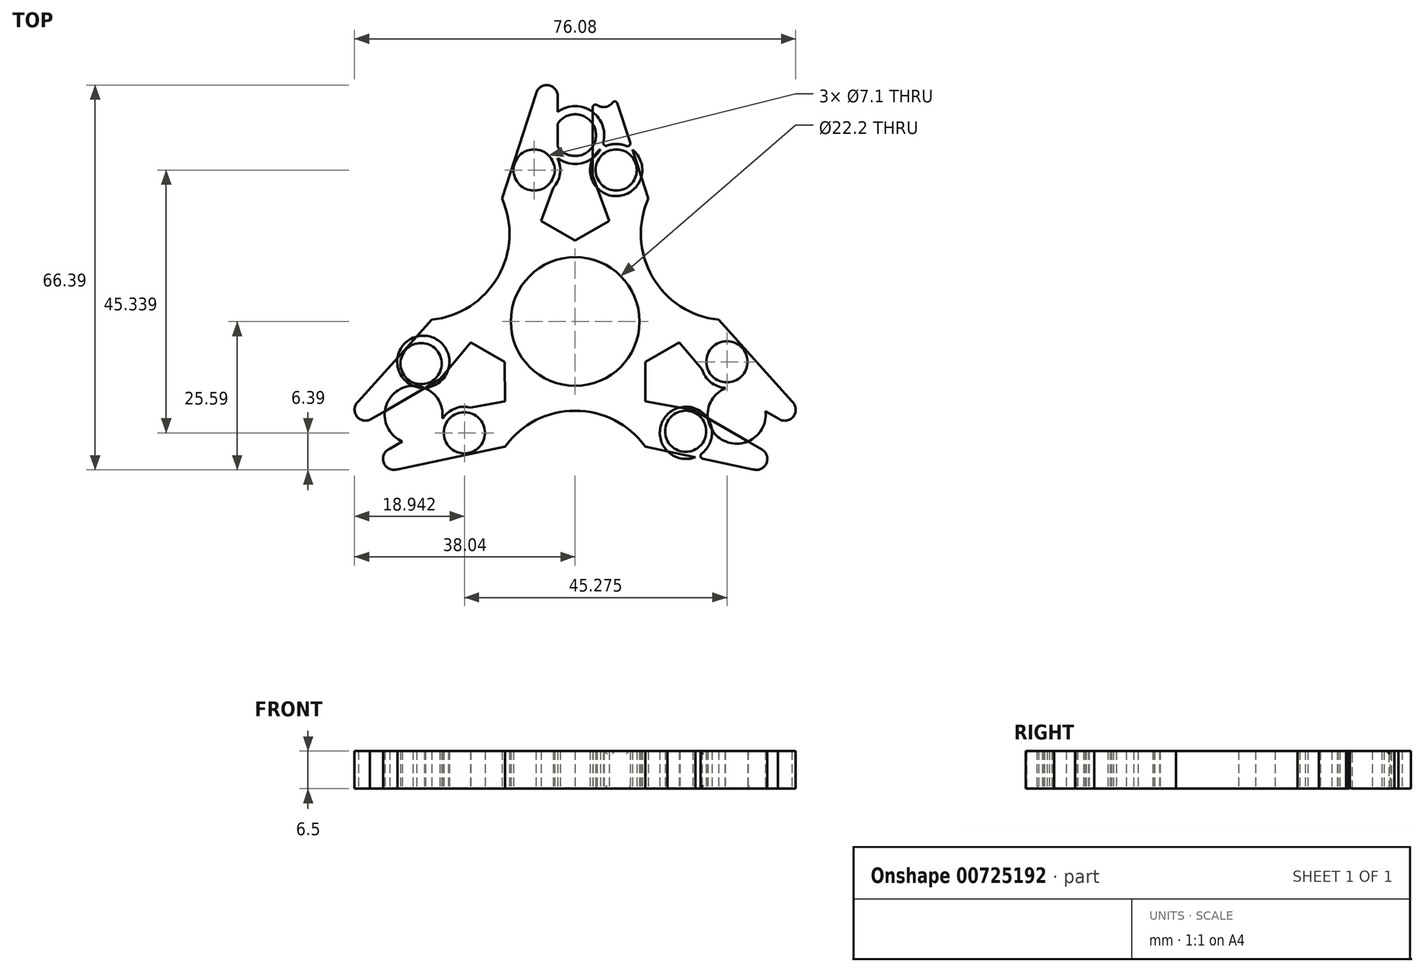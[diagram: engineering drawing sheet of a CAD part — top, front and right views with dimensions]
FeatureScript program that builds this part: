
annotation { "Feature Type Name" : "Feature", "Feature Type Description" : "" }
export const myFeature = defineFeature(function(context is Context, id is Id, definition is map)
    precondition{}
    {
        {
            var Q0;
            Q0=qCreatedBy(makeId("Top.planeOp"),FACE);
            var sketch = newSketch(context, id + "F0", { "sketchPlane" : qUnion([Q0])});
            skCircle(sketch, "E0", {"center": v(0, 0) * mm, "radius": 11.1 * mm});
            skCircle(sketch, "E1", {"center": v(0, 0) * mm, "radius": 14 * mm});
            skPoint(sketch, "E2", {"position": v(-12.63, 21.25) * mm});
            skPoint(sketch, "E3", {"position": v(-6.76, 39.27) * mm});
            skPoint(sketch, "E4.MirrorP", {"position": v(6.76, 39.27) * mm});
            skPoint(sketch, "E5.MirrorP", {"position": v(12.63, 21.25) * mm});
            skLineSegment(sketch, "E6", {"start": v(-12.63, 21.25) * mm, "end": v(-6.76, 39.27) * mm});
            skLineSegment(sketch, "E7", {"start": v(6.76, 39.27) * mm, "end": v(12.63, 21.25) * mm});
            skPoint(sketch, "E8", {"position": v(-3.02, 39.15) * mm});
            skPoint(sketch, "E9", {"position": v(-3.02, 25.17) * mm});
            skPoint(sketch, "E10", {"position": v(-5.89, 17.35) * mm});
            skPoint(sketch, "E11", {"position": v(0, 14) * mm});
            skPoint(sketch, "E12.MirrorP", {"position": v(3.02, 39.15) * mm});
            skPoint(sketch, "E13.MirrorP", {"position": v(3.02, 25.17) * mm});
            skPoint(sketch, "E14.MirrorP", {"position": v(5.89, 17.35) * mm});
            skCircle(sketch, "E15", {"center": v(-4.9, 38.9) * mm, "radius": 1.9 * mm});
            skPoint(sketch, "E15.third.point", {"position": v(-3.58, 37.54) * mm});
            skCircle(sketch, "E16.MirrorC", {"center": v(4.9, 38.9) * mm, "radius": 1.9 * mm});
            skLineSegment(sketch, "E17", {"start": v(-3.02, 39.15) * mm, "end": v(-3.02, 25.17) * mm});
            skLineSegment(sketch, "E18", {"start": v(-5.89, 17.35) * mm, "end": v(-3.02, 25.17) * mm});
            skLineSegment(sketch, "E19", {"start": v(0, 14) * mm, "end": v(-5.89, 17.35) * mm});
            skLineSegment(sketch, "E20", {"start": v(0, 14) * mm, "end": v(5.89, 17.35) * mm});
            skLineSegment(sketch, "E21", {"start": v(3.02, 25.17) * mm, "end": v(5.89, 17.35) * mm});
            skLineSegment(sketch, "E22", {"start": v(3.02, 25.17) * mm, "end": v(3.02, 39.15) * mm});
            skCircle(sketch, "E23", {"center": v(-7.08, 26.14) * mm, "radius": 3.55 * mm});
            skCircle(sketch, "E24.MirrorC", {"center": v(7.08, 26.14) * mm, "radius": 3.55 * mm});
            skPoint(sketch, "E25.centerSnap0", {"position": v(-2.94, 15.68) * mm});
            skPoint(sketch, "E26", {"position": v(-3.02, 28.1) * mm});
            skPoint(sketch, "E27", {"position": v(-3.02, 34.99) * mm});
            skPoint(sketch, "E28.MirrorP", {"position": v(3.02, 34.99) * mm});
            skPoint(sketch, "E29.MirrorP", {"position": v(3.02, 28.1) * mm});
            skCircle(sketch, "E30", {"center": v(0, 32.16) * mm, "radius": 5 * mm});
            skPoint(sketch, "E30.centerSnap0", {"position": v(-3.02, 32.16) * mm});
            skCircle(sketch, "E31", {"center": v(0, 32.16) * mm, "radius": 3.6 * mm});
            skCircle(sketch, "E32.1.0", {"center": v(-31.24, -23.7) * mm, "radius": 1.9 * mm});
            skCircle(sketch, "E32.2.0", {"center": v(36.14, -15.2) * mm, "radius": 1.9 * mm});
            skCircle(sketch, "E33.1.0", {"center": v(-36.14, -15.2) * mm, "radius": 1.9 * mm});
            skCircle(sketch, "E33.2.0", {"center": v(31.24, -23.7) * mm, "radius": 1.9 * mm});
            skLineSegment(sketch, "E34.1.0", {"start": v(-12.09, -21.56) * mm, "end": v(-30.63, -25.5) * mm});
            skLineSegment(sketch, "E34.2.0", {"start": v(24.72, 0.31) * mm, "end": v(37.39, -13.78) * mm});
            skLineSegment(sketch, "E35.1.0", {"start": v(-37.39, -13.78) * mm, "end": v(-24.72, 0.31) * mm});
            skLineSegment(sketch, "E35.2.0", {"start": v(30.63, -25.5) * mm, "end": v(12.09, -21.56) * mm});
            skCircle(sketch, "E36.1.0", {"center": v(-19.1, -19.2) * mm, "radius": 3.55 * mm});
            skCircle(sketch, "E36.2.0", {"center": v(26.18, -6.94) * mm, "radius": 3.55 * mm});
            skCircle(sketch, "E37.1.1", {"center": v(-26.57, -7.25) * mm, "radius": 3.55 * mm});
            skLineSegment(sketch, "E37.1.3", {"start": v(-23.31, -9.97) * mm, "end": v(-17.97, -3.58) * mm});
            skLineSegment(sketch, "E37.1.4", {"start": v(-12.12, -7) * mm, "end": v(-17.97, -3.58) * mm});
            skLineSegment(sketch, "E37.1.5", {"start": v(-12.12, -7) * mm, "end": v(-12.09, -13.77) * mm});
            skLineSegment(sketch, "E37.1.6", {"start": v(-12.09, -13.77) * mm, "end": v(-20.3, -15.2) * mm});
            skLineSegment(sketch, "E37.1.7", {"start": v(-32.4, -22.19) * mm, "end": v(-20.3, -15.2) * mm});
            skCircle(sketch, "E37.1.8", {"center": v(-27.85, -16.08) * mm, "radius": 5 * mm});
            skCircle(sketch, "E37.1.9", {"center": v(-27.85, -16.08) * mm, "radius": 3.6 * mm});
            skLineSegment(sketch, "E37.1.10", {"start": v(-23.31, -9.97) * mm, "end": v(-35.41, -16.96) * mm});
            skCircle(sketch, "E37.2.1", {"center": v(19.05, -18.93) * mm, "radius": 3.55 * mm});
            skLineSegment(sketch, "E37.2.3", {"start": v(20.3, -15.2) * mm, "end": v(12.09, -13.77) * mm});
            skLineSegment(sketch, "E37.2.4", {"start": v(12.12, -7) * mm, "end": v(12.09, -13.77) * mm});
            skLineSegment(sketch, "E37.2.5", {"start": v(12.12, -7) * mm, "end": v(17.97, -3.58) * mm});
            skLineSegment(sketch, "E37.2.6", {"start": v(17.97, -3.58) * mm, "end": v(23.31, -9.97) * mm});
            skLineSegment(sketch, "E37.2.7", {"start": v(35.41, -16.96) * mm, "end": v(23.31, -9.97) * mm});
            skCircle(sketch, "E37.2.8", {"center": v(27.85, -16.08) * mm, "radius": 5 * mm});
            skCircle(sketch, "E37.2.9", {"center": v(27.85, -16.08) * mm, "radius": 3.6 * mm});
            skLineSegment(sketch, "E37.2.10", {"start": v(20.3, -15.2) * mm, "end": v(32.4, -22.19) * mm});
            skArc(sketch, "E38", {"start": v(-24.72, 0.31) * mm, "mid": v(-13.32, 7.7) * mm, "end": v(-12.63, 21.25) * mm});
            skArc(sketch, "E39.1.0", {"start": v(12.09, -21.56) * mm, "mid": v(0, -15.38) * mm, "end": v(-12.09, -21.56) * mm});
            skArc(sketch, "E39.2.0", {"start": v(12.63, 21.25) * mm, "mid": v(13.32, 7.7) * mm, "end": v(24.72, 0.31) * mm});
            skCircle(sketch, "E40", {"center": v(-7.08, 26.14) * mm, "radius": 4.5 * mm});
            skCircle(sketch, "E41.MirrorC", {"center": v(7.08, 26.14) * mm, "radius": 4.5 * mm});
            skCircle(sketch, "E42.1.0", {"center": v(-19.1, -19.2) * mm, "radius": 4.5 * mm});
            skCircle(sketch, "E42.1.1", {"center": v(-26.18, -6.94) * mm, "radius": 4.5 * mm});
            skCircle(sketch, "E42.2.0", {"center": v(26.18, -6.94) * mm, "radius": 4.5 * mm});
            skCircle(sketch, "E42.2.1", {"center": v(19.1, -19.2) * mm, "radius": 4.5 * mm});
            skSolve(sketch);
        }
        {
            var Q0;
            {var subQ0=sQuery(id+"F0.wireOp",EDGE,"E35.1.0");var subQ1=sQuery(id+"F0.wireOp",EDGE,"E33.1.0");var subQ2=makeQuery(id+"F0.imprint","INTERSECT",VERTEX,{"derivedFrom":[subQ1,subQ0]});Q0=makeQuery(id+"F0.imprint","IMPRINT",FACE,{"disambiguationData":[TD([[makeQuery(id+"F0.imprint","IMPRINT",EDGE,{"disambiguationData":[TD([[subQ2,-1.0]])],"derivedFrom":subQ1}),1.0]])]});}
            var Q1;
            {var subQ0=sQuery(id+"F0.wireOp",EDGE,"E37.1.5");Q1=makeQuery(id+"F0.imprint","IMPRINT",FACE,{"disambiguationData":[TD([[makeQuery(id+"F0.imprint","IMPRINT",EDGE,{"derivedFrom":subQ0}),1.0]])]});}
            var Q2;
            {var subQ0=sQuery(id+"F0.wireOp",EDGE,"E35.2.0");var subQ1=sQuery(id+"F0.wireOp",EDGE,"E33.2.0");var subQ2=makeQuery(id+"F0.imprint","INTERSECT",VERTEX,{"derivedFrom":[subQ1,subQ0]});Q2=makeQuery(id+"F0.imprint","IMPRINT",FACE,{"disambiguationData":[TD([[makeQuery(id+"F0.imprint","IMPRINT",EDGE,{"disambiguationData":[TD([[subQ2,-1.0]])],"derivedFrom":subQ1}),1.0]])]});}
            var Q3;
            {var subQ5=sQuery(id+"F0.wireOp",EDGE,"E15");var subQ7=sQuery(id+"F0.wireOp",EDGE,"E6");var subQ8=makeQuery(id+"F0.imprint","INTERSECT",VERTEX,{"derivedFrom":[subQ7,subQ5]});Q3=makeQuery(id+"F0.imprint","IMPRINT",FACE,{"disambiguationData":[TD([[makeQuery(id+"F0.imprint","IMPRINT",EDGE,{"disambiguationData":[TD([[subQ8,1.0]])],"derivedFrom":subQ7}),-1.0]])]});}
            var Q4;
            {var subQ0=sQuery(id+"F0.wireOp",EDGE,"E19");Q4=makeQuery(id+"F0.imprint","IMPRINT",FACE,{"disambiguationData":[TD([[makeQuery(id+"F0.imprint","IMPRINT",EDGE,{"derivedFrom":subQ0}),1.0]])]});}
            var Q5;
            {var subQ0=sQuery(id+"F0.wireOp",EDGE,"E37.1.9");var subQ1=sQuery(id+"F0.wireOp",EDGE,"E37.1.7");var subQ2=makeQuery(id+"F0.imprint","INTERSECT",VERTEX,{"disambiguationData":[OD(1.0)],"derivedFrom":[subQ1,subQ0]});Q5=makeQuery(id+"F0.imprint","IMPRINT",FACE,{"disambiguationData":[TD([[makeQuery(id+"F0.imprint","IMPRINT",EDGE,{"disambiguationData":[TD([[subQ2,-1.0]])],"derivedFrom":subQ1}),1.0]])]});}
            var Q6;
            {var subQ0=sQuery(id+"F0.wireOp",EDGE,"E37.1.8");var subQ1=sQuery(id+"F0.wireOp",EDGE,"E37.1.7");var subQ2=makeQuery(id+"F0.imprint","INTERSECT",VERTEX,{"disambiguationData":[OD(0.0)],"derivedFrom":[subQ1,subQ0]});Q6=makeQuery(id+"F0.imprint","IMPRINT",FACE,{"disambiguationData":[TD([[makeQuery(id+"F0.imprint","IMPRINT",EDGE,{"disambiguationData":[TD([[subQ2,-1.0]])],"derivedFrom":subQ1}),1.0]])]});}
            var Q7;
            {var subQ0=sQuery(id+"F0.wireOp",EDGE,"E42.1.1");var subQ1=sQuery(id+"F0.wireOp",EDGE,"E35.1.0");var subQ2=makeQuery(id+"F0.imprint","INTERSECT",VERTEX,{"disambiguationData":[OD(0.0)],"derivedFrom":[subQ1,subQ0]});Q7=makeQuery(id+"F0.imprint","IMPRINT",FACE,{"disambiguationData":[TD([[makeQuery(id+"F0.imprint","IMPRINT",EDGE,{"disambiguationData":[TD([[subQ2,-1.0]])],"derivedFrom":subQ1}),1.0]])]});}
            var Q8;
            {var subQ0=sQuery(id+"F0.wireOp",EDGE,"E31");var subQ1=sQuery(id+"F0.wireOp",EDGE,"E17");var subQ2=makeQuery(id+"F0.imprint","INTERSECT",VERTEX,{"disambiguationData":[OD(1.0)],"derivedFrom":[subQ1,subQ0]});Q8=makeQuery(id+"F0.imprint","IMPRINT",FACE,{"disambiguationData":[TD([[makeQuery(id+"F0.imprint","IMPRINT",EDGE,{"disambiguationData":[TD([[subQ2,-1.0]])],"derivedFrom":subQ1}),1.0]])]});}
            var Q9;
            {var subQ0=sQuery(id+"F0.wireOp",EDGE,"E20");Q9=makeQuery(id+"F0.imprint","IMPRINT",FACE,{"disambiguationData":[TD([[makeQuery(id+"F0.imprint","IMPRINT",EDGE,{"derivedFrom":subQ0}),-1.0]])]});}
            var Q10;
            {var subQ0=sQuery(id+"F0.wireOp",EDGE,"E37.2.10");var subQ1=sQuery(id+"F0.wireOp",EDGE,"E37.2.8");var subQ2=makeQuery(id+"F0.imprint","INTERSECT",VERTEX,{"disambiguationData":[OD(1.0)],"derivedFrom":[subQ1,subQ0]});Q10=makeQuery(id+"F0.imprint","IMPRINT",FACE,{"disambiguationData":[TD([[makeQuery(id+"F0.imprint","IMPRINT",EDGE,{"disambiguationData":[TD([[subQ2,-1.0]])],"derivedFrom":subQ1}),1.0]])]});}
            var Q11;
            Q11=makeQuery(id+"F0.imprint","IMPRINT",FACE,{"disambiguationData":[TD([[makeQuery(id+"F0.imprint","IMPRINT",EDGE,{"derivedFrom":sQuery(id+"F0.wireOp",EDGE,"E37.1.1")}),1.0]])]});
            var Q12;
            {var subQ0=sQuery(id+"F0.wireOp",EDGE,"E37.2.8");var subQ1=sQuery(id+"F0.wireOp",EDGE,"E37.2.7");var subQ6=makeQuery(id+"F0.imprint","INTERSECT",VERTEX,{"disambiguationData":[OD(0.0)],"derivedFrom":[subQ1,subQ0]});Q12=makeQuery(id+"F0.imprint","IMPRINT",FACE,{"disambiguationData":[TD([[makeQuery(id+"F0.imprint","IMPRINT",EDGE,{"disambiguationData":[TD([[subQ6,-1.0]])],"derivedFrom":subQ1}),-1.0]])]});}
            var Q13;
            {var subQ5=sQuery(id+"F0.wireOp",EDGE,"E16.MirrorC");var subQ7=sQuery(id+"F0.wireOp",EDGE,"E7");var subQ8=makeQuery(id+"F0.imprint","INTERSECT",VERTEX,{"derivedFrom":[subQ7,subQ5]});Q13=makeQuery(id+"F0.imprint","IMPRINT",FACE,{"disambiguationData":[TD([[makeQuery(id+"F0.imprint","IMPRINT",EDGE,{"disambiguationData":[TD([[subQ8,-1.0]])],"derivedFrom":subQ7}),-1.0]])]});}
            var Q14;
            Q14=makeQuery(id+"F0.imprint","IMPRINT",FACE,{"disambiguationData":[TD([[makeQuery(id+"F0.imprint","IMPRINT",EDGE,{"derivedFrom":sQuery(id+"F0.wireOp",EDGE,"E36.1.0")}),-1.0]])]});
            var Q15;
            {var subQ0=sQuery(id+"F0.wireOp",EDGE,"E30");var subQ1=sQuery(id+"F0.wireOp",EDGE,"E22");var subQ5=makeQuery(id+"F0.imprint","INTERSECT",VERTEX,{"disambiguationData":[OD(1.0)],"derivedFrom":[subQ1,subQ0]});Q15=makeQuery(id+"F0.imprint","IMPRINT",FACE,{"disambiguationData":[TD([[makeQuery(id+"F0.imprint","IMPRINT",EDGE,{"disambiguationData":[TD([[subQ5,-1.0]])],"derivedFrom":subQ1}),-1.0]])]});}
            var Q16;
            {var subQ0=sQuery(id+"F0.wireOp",EDGE,"E37.1.8");var subQ1=sQuery(id+"F0.wireOp",EDGE,"E37.1.7");var subQ5=makeQuery(id+"F0.imprint","INTERSECT",VERTEX,{"disambiguationData":[OD(0.0)],"derivedFrom":[subQ1,subQ0]});Q16=makeQuery(id+"F0.imprint","IMPRINT",FACE,{"disambiguationData":[TD([[makeQuery(id+"F0.imprint","IMPRINT",EDGE,{"disambiguationData":[TD([[subQ5,-1.0]])],"derivedFrom":subQ1}),-1.0]])]});}
            var Q17;
            {var subQ1=sQuery(id+"F0.wireOp",EDGE,"E32.2.0");var subQ5=sQuery(id+"F0.wireOp",EDGE,"E34.2.0");var subQ6=makeQuery(id+"F0.imprint","INTERSECT",VERTEX,{"derivedFrom":[subQ1,subQ5]});Q17=makeQuery(id+"F0.imprint","IMPRINT",FACE,{"disambiguationData":[TD([[makeQuery(id+"F0.imprint","IMPRINT",EDGE,{"disambiguationData":[TD([[subQ6,-1.0]])],"derivedFrom":subQ1}),-1.0]])]});}
            var Q18;
            Q18=makeQuery(id+"F0.imprint","IMPRINT",FACE,{"disambiguationData":[TD([[makeQuery(id+"F0.imprint","IMPRINT",EDGE,{"derivedFrom":sQuery(id+"F0.wireOp",EDGE,"E0")}),-1.0]])]});
            var Q19;
            {var subQ1=sQuery(id+"F0.wireOp",EDGE,"E32.1.0");var subQ5=sQuery(id+"F0.wireOp",EDGE,"E34.1.0");var subQ6=makeQuery(id+"F0.imprint","INTERSECT",VERTEX,{"derivedFrom":[subQ1,subQ5]});Q19=makeQuery(id+"F0.imprint","IMPRINT",FACE,{"disambiguationData":[TD([[makeQuery(id+"F0.imprint","IMPRINT",EDGE,{"disambiguationData":[TD([[subQ6,-1.0]])],"derivedFrom":subQ1}),-1.0]])]});}
            var Q20;
            Q20=makeQuery(id+"F0.imprint","IMPRINT",FACE,{"disambiguationData":[TD([[makeQuery(id+"F0.imprint","IMPRINT",EDGE,{"derivedFrom":sQuery(id+"F0.wireOp",EDGE,"E37.2.1")}),1.0]])]});
            var Q21;
            {var subQ0=sQuery(id+"F0.wireOp",EDGE,"E37.2.9");var subQ1=sQuery(id+"F0.wireOp",EDGE,"E37.2.7");var subQ2=makeQuery(id+"F0.imprint","INTERSECT",VERTEX,{"disambiguationData":[OD(1.0)],"derivedFrom":[subQ1,subQ0]});Q21=makeQuery(id+"F0.imprint","IMPRINT",FACE,{"disambiguationData":[TD([[makeQuery(id+"F0.imprint","IMPRINT",EDGE,{"disambiguationData":[TD([[subQ2,-1.0]])],"derivedFrom":subQ1}),1.0]])]});}
            var Q22;
            {var subQ0=sQuery(id+"F0.wireOp",EDGE,"E37.2.8");var subQ1=sQuery(id+"F0.wireOp",EDGE,"E37.2.7");var subQ2=makeQuery(id+"F0.imprint","INTERSECT",VERTEX,{"disambiguationData":[OD(0.0)],"derivedFrom":[subQ1,subQ0]});Q22=makeQuery(id+"F0.imprint","IMPRINT",FACE,{"disambiguationData":[TD([[makeQuery(id+"F0.imprint","IMPRINT",EDGE,{"disambiguationData":[TD([[subQ2,-1.0]])],"derivedFrom":subQ1}),1.0]])]});}
            var Q23;
            {var subQ0=sQuery(id+"F0.wireOp",EDGE,"E37.1.10");var subQ1=sQuery(id+"F0.wireOp",EDGE,"E37.1.8");var subQ2=makeQuery(id+"F0.imprint","INTERSECT",VERTEX,{"disambiguationData":[OD(1.0)],"derivedFrom":[subQ1,subQ0]});Q23=makeQuery(id+"F0.imprint","IMPRINT",FACE,{"disambiguationData":[TD([[makeQuery(id+"F0.imprint","IMPRINT",EDGE,{"disambiguationData":[TD([[subQ2,-1.0]])],"derivedFrom":subQ1}),1.0]])]});}
            var Q24;
            {var subQ0=sQuery(id+"F0.wireOp",EDGE,"E42.1.1");var subQ1=sQuery(id+"F0.wireOp",EDGE,"E37.1.8");var subQ2=makeQuery(id+"F0.imprint","INTERSECT",VERTEX,{"disambiguationData":[OD(0.0)],"derivedFrom":[subQ1,subQ0]});Q24=makeQuery(id+"F0.imprint","IMPRINT",FACE,{"disambiguationData":[TD([[makeQuery(id+"F0.imprint","IMPRINT",EDGE,{"disambiguationData":[TD([[subQ2,-1.0]])],"derivedFrom":subQ1}),1.0]])]});}
            var Q25;
            {var subQ0=sQuery(id+"F0.wireOp",EDGE,"E33.1.0");var subQ1=makeQuery(id+"F0.imprint","INTERSECT",VERTEX,{"derivedFrom":[subQ0,sQuery(id+"F0.wireOp",EDGE,"E35.1.0")]});Q25=makeQuery(id+"F0.imprint","IMPRINT",FACE,{"disambiguationData":[TD([[makeQuery(id+"F0.imprint","IMPRINT",EDGE,{"disambiguationData":[TD([[subQ1,1.0]])],"derivedFrom":subQ0}),-1.0]])]});}
            var Q26;
            {var subQ0=sQuery(id+"F0.wireOp",EDGE,"E37.1.9");var subQ1=sQuery(id+"F0.wireOp",EDGE,"E37.1.7");var subQ2=makeQuery(id+"F0.imprint","INTERSECT",VERTEX,{"disambiguationData":[OD(0.0)],"derivedFrom":[subQ1,subQ0]});Q26=makeQuery(id+"F0.imprint","IMPRINT",FACE,{"disambiguationData":[TD([[makeQuery(id+"F0.imprint","IMPRINT",EDGE,{"disambiguationData":[TD([[subQ2,-1.0]])],"derivedFrom":subQ1}),-1.0]])]});}
            var Q27;
            {var subQ0=sQuery(id+"F0.wireOp",EDGE,"E42.2.0");var subQ1=sQuery(id+"F0.wireOp",EDGE,"E37.2.8");var subQ2=makeQuery(id+"F0.imprint","INTERSECT",VERTEX,{"disambiguationData":[OD(0.0)],"derivedFrom":[subQ1,subQ0]});Q27=makeQuery(id+"F0.imprint","IMPRINT",FACE,{"disambiguationData":[TD([[makeQuery(id+"F0.imprint","IMPRINT",EDGE,{"disambiguationData":[TD([[subQ2,-1.0]])],"derivedFrom":subQ1}),1.0]])]});}
            var Q28;
            {var subQ0=sQuery(id+"F0.wireOp",EDGE,"E33.2.0");var subQ1=makeQuery(id+"F0.imprint","INTERSECT",VERTEX,{"derivedFrom":[subQ0,sQuery(id+"F0.wireOp",EDGE,"E35.2.0")]});Q28=makeQuery(id+"F0.imprint","IMPRINT",FACE,{"disambiguationData":[TD([[makeQuery(id+"F0.imprint","IMPRINT",EDGE,{"disambiguationData":[TD([[subQ1,1.0]])],"derivedFrom":subQ0}),-1.0]])]});}
            var Q29;
            {var subQ0=sQuery(id+"F0.wireOp",EDGE,"E30");var subQ1=sQuery(id+"F0.wireOp",EDGE,"E17");var subQ2=makeQuery(id+"F0.imprint","INTERSECT",VERTEX,{"disambiguationData":[OD(0.0)],"derivedFrom":[subQ1,subQ0]});Q29=makeQuery(id+"F0.imprint","IMPRINT",FACE,{"disambiguationData":[TD([[makeQuery(id+"F0.imprint","IMPRINT",EDGE,{"disambiguationData":[TD([[subQ2,-1.0]])],"derivedFrom":subQ1}),1.0]])]});}
            var Q30;
            {var subQ0=sQuery(id+"F0.wireOp",EDGE,"E37.2.10");var subQ1=sQuery(id+"F0.wireOp",EDGE,"E37.2.9");var subQ2=makeQuery(id+"F0.imprint","INTERSECT",VERTEX,{"disambiguationData":[OD(0.0)],"derivedFrom":[subQ1,subQ0]});Q30=makeQuery(id+"F0.imprint","IMPRINT",FACE,{"disambiguationData":[TD([[makeQuery(id+"F0.imprint","IMPRINT",EDGE,{"disambiguationData":[TD([[subQ2,1.0]])],"derivedFrom":subQ1}),1.0]])]});}
            var Q31;
            {var subQ0=sQuery(id+"F0.wireOp",EDGE,"E42.1.0");var subQ1=sQuery(id+"F0.wireOp",EDGE,"E37.1.8");var subQ2=makeQuery(id+"F0.imprint","INTERSECT",VERTEX,{"disambiguationData":[OD(0.0)],"derivedFrom":[subQ1,subQ0]});Q31=makeQuery(id+"F0.imprint","IMPRINT",FACE,{"disambiguationData":[TD([[makeQuery(id+"F0.imprint","IMPRINT",EDGE,{"disambiguationData":[TD([[subQ2,-1.0]])],"derivedFrom":subQ1}),1.0]])]});}
            var Q32;
            {var subQ0=sQuery(id+"F0.wireOp",EDGE,"E37.1.10");var subQ1=sQuery(id+"F0.wireOp",EDGE,"E33.1.0");var subQ2=makeQuery(id+"F0.imprint","INTERSECT",VERTEX,{"disambiguationData":[OD(0.0)],"derivedFrom":[subQ1,subQ0]});Q32=makeQuery(id+"F0.imprint","IMPRINT",FACE,{"disambiguationData":[TD([[makeQuery(id+"F0.imprint","IMPRINT",EDGE,{"disambiguationData":[TD([[subQ2,1.0]])],"derivedFrom":subQ1}),-1.0]])]});}
            var Q33;
            {var subQ0=sQuery(id+"F0.wireOp",EDGE,"E37.1.10");var subQ1=sQuery(id+"F0.wireOp",EDGE,"E37.1.8");var subQ2=makeQuery(id+"F0.imprint","INTERSECT",VERTEX,{"disambiguationData":[OD(1.0)],"derivedFrom":[subQ1,subQ0]});Q33=makeQuery(id+"F0.imprint","IMPRINT",FACE,{"disambiguationData":[TD([[makeQuery(id+"F0.imprint","IMPRINT",EDGE,{"disambiguationData":[TD([[subQ2,-1.0]])],"derivedFrom":subQ1}),-1.0]])]});}
            var Q34;
            Q34=makeQuery(id+"F0.imprint","IMPRINT",FACE,{"disambiguationData":[TD([[makeQuery(id+"F0.imprint","IMPRINT",EDGE,{"derivedFrom":sQuery(id+"F0.wireOp",EDGE,"E24.MirrorC")}),1.0]])]});
            var Q35;
            {var subQ0=sQuery(id+"F0.wireOp",EDGE,"E42.1.0");var subQ1=sQuery(id+"F0.wireOp",EDGE,"E34.1.0");var subQ2=makeQuery(id+"F0.imprint","INTERSECT",VERTEX,{"disambiguationData":[OD(0.0)],"derivedFrom":[subQ1,subQ0]});Q35=makeQuery(id+"F0.imprint","IMPRINT",FACE,{"disambiguationData":[TD([[makeQuery(id+"F0.imprint","IMPRINT",EDGE,{"disambiguationData":[TD([[subQ2,-1.0]])],"derivedFrom":subQ1}),1.0]])]});}
            var Q36;
            {var subQ0=sQuery(id+"F0.wireOp",EDGE,"E32.2.0");var subQ1=makeQuery(id+"F0.imprint","INTERSECT",VERTEX,{"derivedFrom":[subQ0,sQuery(id+"F0.wireOp",EDGE,"E34.2.0")]});Q36=makeQuery(id+"F0.imprint","IMPRINT",FACE,{"disambiguationData":[TD([[makeQuery(id+"F0.imprint","IMPRINT",EDGE,{"disambiguationData":[TD([[subQ1,1.0]])],"derivedFrom":subQ0}),1.0]])]});}
            var Q37;
            {var subQ0=sQuery(id+"F0.wireOp",EDGE,"E37.1.7");var subQ1=sQuery(id+"F0.wireOp",EDGE,"E37.1.6");var subQ2=makeQuery(id+"F0.imprint","INTERSECT",VERTEX,{"derivedFrom":[subQ1,subQ0]});Q37=makeQuery(id+"F0.imprint","IMPRINT",FACE,{"disambiguationData":[TD([[makeQuery(id+"F0.imprint","IMPRINT",EDGE,{"disambiguationData":[TD([[subQ2,1.0]])],"derivedFrom":subQ1}),-1.0]])]});}
            var Q38;
            Q38=makeQuery(id+"F0.imprint","IMPRINT",FACE,{"disambiguationData":[TD([[makeQuery(id+"F0.imprint","IMPRINT",EDGE,{"derivedFrom":sQuery(id+"F0.wireOp",EDGE,"E23")}),-1.0]])]});
            var Q39;
            {var subQ0=sQuery(id+"F0.wireOp",EDGE,"E41.MirrorC");var subQ1=sQuery(id+"F0.wireOp",EDGE,"E7");var subQ2=makeQuery(id+"F0.imprint","INTERSECT",VERTEX,{"disambiguationData":[OD(0.0)],"derivedFrom":[subQ1,subQ0]});Q39=makeQuery(id+"F0.imprint","IMPRINT",FACE,{"disambiguationData":[TD([[makeQuery(id+"F0.imprint","IMPRINT",EDGE,{"disambiguationData":[TD([[subQ2,-1.0]])],"derivedFrom":subQ1}),1.0]])]});}
            var Q40;
            {var subQ0=sQuery(id+"F0.wireOp",EDGE,"E42.2.1");var subQ1=sQuery(id+"F0.wireOp",EDGE,"E37.2.8");var subQ2=makeQuery(id+"F0.imprint","INTERSECT",VERTEX,{"disambiguationData":[OD(0.0)],"derivedFrom":[subQ1,subQ0]});Q40=makeQuery(id+"F0.imprint","IMPRINT",FACE,{"disambiguationData":[TD([[makeQuery(id+"F0.imprint","IMPRINT",EDGE,{"disambiguationData":[TD([[subQ2,-1.0]])],"derivedFrom":subQ1}),1.0]])]});}
            var Q41;
            {var subQ0=sQuery(id+"F0.wireOp",EDGE,"E37.1.10");var subQ1=sQuery(id+"F0.wireOp",EDGE,"E37.1.3");var subQ2=makeQuery(id+"F0.imprint","INTERSECT",VERTEX,{"derivedFrom":[subQ1,subQ0]});Q41=makeQuery(id+"F0.imprint","IMPRINT",FACE,{"disambiguationData":[TD([[makeQuery(id+"F0.imprint","IMPRINT",EDGE,{"disambiguationData":[TD([[subQ2,-1.0]])],"derivedFrom":subQ1}),-1.0]])]});}
            var Q42;
            {var subQ0=sQuery(id+"F0.wireOp",EDGE,"E37.1.8");var subQ1=sQuery(id+"F0.wireOp",EDGE,"E37.1.7");var subQ2=makeQuery(id+"F0.imprint","INTERSECT",VERTEX,{"disambiguationData":[OD(1.0)],"derivedFrom":[subQ1,subQ0]});Q42=makeQuery(id+"F0.imprint","IMPRINT",FACE,{"disambiguationData":[TD([[makeQuery(id+"F0.imprint","IMPRINT",EDGE,{"disambiguationData":[TD([[subQ2,-1.0]])],"derivedFrom":subQ1}),-1.0]])]});}
            var Q43;
            {var subQ0=sQuery(id+"F0.wireOp",EDGE,"E37.2.10");var subQ1=sQuery(id+"F0.wireOp",EDGE,"E37.2.3");var subQ2=makeQuery(id+"F0.imprint","INTERSECT",VERTEX,{"derivedFrom":[subQ1,subQ0]});Q43=makeQuery(id+"F0.imprint","IMPRINT",FACE,{"disambiguationData":[TD([[makeQuery(id+"F0.imprint","IMPRINT",EDGE,{"disambiguationData":[TD([[subQ2,-1.0]])],"derivedFrom":subQ1}),-1.0]])]});}
            var Q44;
            {var subQ0=sQuery(id+"F0.wireOp",EDGE,"E37.1.10");var subQ1=sQuery(id+"F0.wireOp",EDGE,"E37.1.9");var subQ2=makeQuery(id+"F0.imprint","INTERSECT",VERTEX,{"disambiguationData":[OD(0.0)],"derivedFrom":[subQ1,subQ0]});Q44=makeQuery(id+"F0.imprint","IMPRINT",FACE,{"disambiguationData":[TD([[makeQuery(id+"F0.imprint","IMPRINT",EDGE,{"disambiguationData":[TD([[subQ2,1.0]])],"derivedFrom":subQ1}),1.0]])]});}
            var Q45;
            {var subQ0=sQuery(id+"F0.wireOp",EDGE,"E32.1.0");var subQ1=makeQuery(id+"F0.imprint","INTERSECT",VERTEX,{"derivedFrom":[subQ0,sQuery(id+"F0.wireOp",EDGE,"E34.1.0")]});Q45=makeQuery(id+"F0.imprint","IMPRINT",FACE,{"disambiguationData":[TD([[makeQuery(id+"F0.imprint","IMPRINT",EDGE,{"disambiguationData":[TD([[subQ1,1.0]])],"derivedFrom":subQ0}),1.0]])]});}
            var Q46;
            {var subQ0=sQuery(id+"F0.wireOp",EDGE,"E31");var subQ1=sQuery(id+"F0.wireOp",EDGE,"E17");var subQ2=makeQuery(id+"F0.imprint","INTERSECT",VERTEX,{"disambiguationData":[OD(0.0)],"derivedFrom":[subQ1,subQ0]});Q46=makeQuery(id+"F0.imprint","IMPRINT",FACE,{"disambiguationData":[TD([[makeQuery(id+"F0.imprint","IMPRINT",EDGE,{"disambiguationData":[TD([[subQ2,-1.0]])],"derivedFrom":subQ1}),-1.0]])]});}
            var Q47;
            Q47=makeQuery(id+"F0.imprint","IMPRINT",FACE,{"disambiguationData":[TD([[makeQuery(id+"F0.imprint","IMPRINT",EDGE,{"derivedFrom":sQuery(id+"F0.wireOp",EDGE,"E36.2.0")}),-1.0]])]});
            var Q48;
            {var subQ0=sQuery(id+"F0.wireOp",EDGE,"E30");var subQ1=sQuery(id+"F0.wireOp",EDGE,"E17");var subQ5=makeQuery(id+"F0.imprint","INTERSECT",VERTEX,{"disambiguationData":[OD(0.0)],"derivedFrom":[subQ1,subQ0]});Q48=makeQuery(id+"F0.imprint","IMPRINT",FACE,{"disambiguationData":[TD([[makeQuery(id+"F0.imprint","IMPRINT",EDGE,{"disambiguationData":[TD([[subQ5,-1.0]])],"derivedFrom":subQ1}),-1.0]])]});}
            var Q49;
            {var subQ0=sQuery(id+"F0.wireOp",EDGE,"E37.2.9");var subQ1=sQuery(id+"F0.wireOp",EDGE,"E37.2.7");var subQ2=makeQuery(id+"F0.imprint","INTERSECT",VERTEX,{"disambiguationData":[OD(0.0)],"derivedFrom":[subQ1,subQ0]});Q49=makeQuery(id+"F0.imprint","IMPRINT",FACE,{"disambiguationData":[TD([[makeQuery(id+"F0.imprint","IMPRINT",EDGE,{"disambiguationData":[TD([[subQ2,-1.0]])],"derivedFrom":subQ1}),-1.0]])]});}
            var Q50;
            {var subQ0=sQuery(id+"F0.wireOp",EDGE,"E42.2.0");var subQ1=sQuery(id+"F0.wireOp",EDGE,"E34.2.0");var subQ2=makeQuery(id+"F0.imprint","INTERSECT",VERTEX,{"disambiguationData":[OD(0.0)],"derivedFrom":[subQ1,subQ0]});Q50=makeQuery(id+"F0.imprint","IMPRINT",FACE,{"disambiguationData":[TD([[makeQuery(id+"F0.imprint","IMPRINT",EDGE,{"disambiguationData":[TD([[subQ2,-1.0]])],"derivedFrom":subQ1}),1.0]])]});}
            var Q51;
            {var subQ0=sQuery(id+"F0.wireOp",EDGE,"E42.2.1");var subQ1=sQuery(id+"F0.wireOp",EDGE,"E35.2.0");var subQ2=makeQuery(id+"F0.imprint","INTERSECT",VERTEX,{"disambiguationData":[OD(0.0)],"derivedFrom":[subQ1,subQ0]});Q51=makeQuery(id+"F0.imprint","IMPRINT",FACE,{"disambiguationData":[TD([[makeQuery(id+"F0.imprint","IMPRINT",EDGE,{"disambiguationData":[TD([[subQ2,-1.0]])],"derivedFrom":subQ1}),1.0]])]});}
            var Q52;
            {var subQ0=sQuery(id+"F0.wireOp",EDGE,"E40");var subQ1=sQuery(id+"F0.wireOp",EDGE,"E6");var subQ2=makeQuery(id+"F0.imprint","INTERSECT",VERTEX,{"disambiguationData":[OD(0.0)],"derivedFrom":[subQ1,subQ0]});Q52=makeQuery(id+"F0.imprint","IMPRINT",FACE,{"disambiguationData":[TD([[makeQuery(id+"F0.imprint","IMPRINT",EDGE,{"disambiguationData":[TD([[subQ2,-1.0]])],"derivedFrom":subQ1}),1.0]])]});}
            var Q53;
            {var subQ0=sQuery(id+"F0.wireOp",EDGE,"E15");var subQ1=makeQuery(id+"F0.imprint","INTERSECT",VERTEX,{"derivedFrom":[sQuery(id+"F0.wireOp",EDGE,"E6"),subQ0]});Q53=makeQuery(id+"F0.imprint","IMPRINT",FACE,{"disambiguationData":[TD([[makeQuery(id+"F0.imprint","IMPRINT",EDGE,{"disambiguationData":[TD([[subQ1,1.0]])],"derivedFrom":subQ0}),1.0]])]});}
            var Q54;
            {var subQ0=sQuery(id+"F0.wireOp",EDGE,"E37.2.8");var subQ1=sQuery(id+"F0.wireOp",EDGE,"E37.2.7");var subQ2=makeQuery(id+"F0.imprint","INTERSECT",VERTEX,{"disambiguationData":[OD(1.0)],"derivedFrom":[subQ1,subQ0]});Q54=makeQuery(id+"F0.imprint","IMPRINT",FACE,{"disambiguationData":[TD([[makeQuery(id+"F0.imprint","IMPRINT",EDGE,{"disambiguationData":[TD([[subQ2,-1.0]])],"derivedFrom":subQ1}),-1.0]])]});}
            var Q55;
            {var subQ0=sQuery(id+"F0.wireOp",EDGE,"E22");var subQ1=sQuery(id+"F0.wireOp",EDGE,"E21");var subQ2=makeQuery(id+"F0.imprint","INTERSECT",VERTEX,{"derivedFrom":[subQ1,subQ0]});Q55=makeQuery(id+"F0.imprint","IMPRINT",FACE,{"disambiguationData":[TD([[makeQuery(id+"F0.imprint","IMPRINT",EDGE,{"disambiguationData":[TD([[subQ2,-1.0]])],"derivedFrom":subQ1}),-1.0]])]});}
            var Q56;
            {var subQ0=sQuery(id+"F0.wireOp",EDGE,"E17");var subQ1=sQuery(id+"F0.wireOp",EDGE,"E15");var subQ2=makeQuery(id+"F0.imprint","INTERSECT",VERTEX,{"disambiguationData":[OD(0.0)],"derivedFrom":[subQ1,subQ0]});Q56=makeQuery(id+"F0.imprint","IMPRINT",FACE,{"disambiguationData":[TD([[makeQuery(id+"F0.imprint","IMPRINT",EDGE,{"disambiguationData":[TD([[subQ2,1.0]])],"derivedFrom":subQ1}),1.0]])]});}
            var Q57;
            {var subQ0=sQuery(id+"F0.wireOp",EDGE,"E37.2.7");var subQ1=sQuery(id+"F0.wireOp",EDGE,"E37.2.6");var subQ2=makeQuery(id+"F0.imprint","INTERSECT",VERTEX,{"derivedFrom":[subQ1,subQ0]});Q57=makeQuery(id+"F0.imprint","IMPRINT",FACE,{"disambiguationData":[TD([[makeQuery(id+"F0.imprint","IMPRINT",EDGE,{"disambiguationData":[TD([[subQ2,1.0]])],"derivedFrom":subQ1}),-1.0]])]});}
            var Q58;
            {var subQ0=sQuery(id+"F0.wireOp",EDGE,"E18");var subQ1=sQuery(id+"F0.wireOp",EDGE,"E17");var subQ2=makeQuery(id+"F0.imprint","INTERSECT",VERTEX,{"derivedFrom":[subQ1,subQ0]});Q58=makeQuery(id+"F0.imprint","IMPRINT",FACE,{"disambiguationData":[TD([[makeQuery(id+"F0.imprint","IMPRINT",EDGE,{"disambiguationData":[TD([[subQ2,1.0]])],"derivedFrom":subQ1}),1.0]])]});}
            var Q59;
            {var subQ0=sQuery(id+"F0.wireOp",EDGE,"E16.MirrorC");var subQ1=makeQuery(id+"F0.imprint","INTERSECT",VERTEX,{"derivedFrom":[sQuery(id+"F0.wireOp",EDGE,"E7"),subQ0]});Q59=makeQuery(id+"F0.imprint","IMPRINT",FACE,{"disambiguationData":[TD([[makeQuery(id+"F0.imprint","IMPRINT",EDGE,{"disambiguationData":[TD([[subQ1,1.0]])],"derivedFrom":subQ0}),-1.0]])]});}
            var Q60;
            {var subQ0=sQuery(id+"F0.wireOp",EDGE,"E41.MirrorC");var subQ1=sQuery(id+"F0.wireOp",EDGE,"E30");var subQ2=makeQuery(id+"F0.imprint","INTERSECT",VERTEX,{"disambiguationData":[OD(0.0)],"derivedFrom":[subQ1,subQ0]});Q60=makeQuery(id+"F0.imprint","IMPRINT",FACE,{"disambiguationData":[TD([[makeQuery(id+"F0.imprint","IMPRINT",EDGE,{"disambiguationData":[TD([[subQ2,-1.0]])],"derivedFrom":subQ1}),1.0]])]});}
            var Q61;
            {var subQ0=sQuery(id+"F0.wireOp",EDGE,"E37.2.10");var subQ1=sQuery(id+"F0.wireOp",EDGE,"E37.2.8");var subQ2=makeQuery(id+"F0.imprint","INTERSECT",VERTEX,{"disambiguationData":[OD(1.0)],"derivedFrom":[subQ1,subQ0]});Q61=makeQuery(id+"F0.imprint","IMPRINT",FACE,{"disambiguationData":[TD([[makeQuery(id+"F0.imprint","IMPRINT",EDGE,{"disambiguationData":[TD([[subQ2,-1.0]])],"derivedFrom":subQ1}),-1.0]])]});}
            var Q62;
            {var subQ0=sQuery(id+"F0.wireOp",EDGE,"E31");var subQ1=sQuery(id+"F0.wireOp",EDGE,"E22");var subQ2=makeQuery(id+"F0.imprint","INTERSECT",VERTEX,{"disambiguationData":[OD(0.0)],"derivedFrom":[subQ1,subQ0]});Q62=makeQuery(id+"F0.imprint","IMPRINT",FACE,{"disambiguationData":[TD([[makeQuery(id+"F0.imprint","IMPRINT",EDGE,{"disambiguationData":[TD([[subQ2,-1.0]])],"derivedFrom":subQ1}),-1.0]])]});}
            var Q63;
            {var subQ0=sQuery(id+"F0.wireOp",EDGE,"E40");var subQ1=sQuery(id+"F0.wireOp",EDGE,"E30");var subQ2=makeQuery(id+"F0.imprint","INTERSECT",VERTEX,{"disambiguationData":[OD(0.0)],"derivedFrom":[subQ1,subQ0]});Q63=makeQuery(id+"F0.imprint","IMPRINT",FACE,{"disambiguationData":[TD([[makeQuery(id+"F0.imprint","IMPRINT",EDGE,{"disambiguationData":[TD([[subQ2,-1.0]])],"derivedFrom":subQ1}),1.0]])]});}
            var Q64;
            {var subQ0=sQuery(id+"F0.wireOp",EDGE,"E37.2.10");var subQ1=sQuery(id+"F0.wireOp",EDGE,"E33.2.0");var subQ2=makeQuery(id+"F0.imprint","INTERSECT",VERTEX,{"disambiguationData":[OD(0.0)],"derivedFrom":[subQ1,subQ0]});Q64=makeQuery(id+"F0.imprint","IMPRINT",FACE,{"disambiguationData":[TD([[makeQuery(id+"F0.imprint","IMPRINT",EDGE,{"disambiguationData":[TD([[subQ2,1.0]])],"derivedFrom":subQ1}),-1.0]])]});}
            var Q65;
            {var subQ0=sQuery(id+"F0.wireOp",EDGE,"E37.2.7");var subQ1=sQuery(id+"F0.wireOp",EDGE,"E32.2.0");var subQ2=makeQuery(id+"F0.imprint","INTERSECT",VERTEX,{"disambiguationData":[OD(0.0)],"derivedFrom":[subQ1,subQ0]});Q65=makeQuery(id+"F0.imprint","IMPRINT",FACE,{"disambiguationData":[TD([[makeQuery(id+"F0.imprint","IMPRINT",EDGE,{"disambiguationData":[TD([[subQ2,1.0]])],"derivedFrom":subQ1}),1.0]])]});}
            var Q66;
            {var subQ0=sQuery(id+"F0.wireOp",EDGE,"E37.1.7");var subQ1=sQuery(id+"F0.wireOp",EDGE,"E32.1.0");var subQ2=makeQuery(id+"F0.imprint","INTERSECT",VERTEX,{"disambiguationData":[OD(0.0)],"derivedFrom":[subQ1,subQ0]});Q66=makeQuery(id+"F0.imprint","IMPRINT",FACE,{"disambiguationData":[TD([[makeQuery(id+"F0.imprint","IMPRINT",EDGE,{"disambiguationData":[TD([[subQ2,1.0]])],"derivedFrom":subQ1}),1.0]])]});}
            var Q67;
            {var subQ0=sQuery(id+"F0.wireOp",EDGE,"E22");var subQ1=sQuery(id+"F0.wireOp",EDGE,"E16.MirrorC");var subQ2=makeQuery(id+"F0.imprint","INTERSECT",VERTEX,{"disambiguationData":[OD(0.0)],"derivedFrom":[subQ1,subQ0]});Q67=makeQuery(id+"F0.imprint","IMPRINT",FACE,{"disambiguationData":[TD([[makeQuery(id+"F0.imprint","IMPRINT",EDGE,{"disambiguationData":[TD([[subQ2,1.0]])],"derivedFrom":subQ1}),-1.0]])]});}
            var Q68;
            {var subQ0=sQuery(id+"F0.wireOp",EDGE,"E41.MirrorC");var subQ1=sQuery(id+"F0.wireOp",EDGE,"E22");var subQ2=makeQuery(id+"F0.imprint","INTERSECT",VERTEX,{"derivedFrom":[subQ1,subQ0]});Q68=makeQuery(id+"F0.imprint","IMPRINT",FACE,{"disambiguationData":[TD([[makeQuery(id+"F0.imprint","IMPRINT",EDGE,{"disambiguationData":[TD([[subQ2,-1.0]])],"derivedFrom":subQ1}),-1.0]])]});}
            var Q69;
            {var subQ0=sQuery(id+"F0.wireOp",EDGE,"E30");var subQ1=sQuery(id+"F0.wireOp",EDGE,"E17");var subQ2=makeQuery(id+"F0.imprint","INTERSECT",VERTEX,{"disambiguationData":[OD(1.0)],"derivedFrom":[subQ1,subQ0]});Q69=makeQuery(id+"F0.imprint","IMPRINT",FACE,{"disambiguationData":[TD([[makeQuery(id+"F0.imprint","IMPRINT",EDGE,{"disambiguationData":[TD([[subQ2,-1.0]])],"derivedFrom":subQ1}),-1.0]])]});}
            extrude(context, id + "F1", {"entities" : qUnion([Q0, Q1, Q2, Q3, Q4, Q5, Q6, Q7, Q8, Q9, Q10, Q11, Q12, Q13, Q14, Q15, Q16, Q17, Q18, Q19, Q20, Q21, Q22, Q23, Q24, Q25, Q26, Q27, Q28, Q29, Q30, Q31, Q32, Q33, Q34, Q35, Q36, Q37, Q38, Q39, Q40, Q41, Q42, Q43, Q44, Q45, Q46, Q47, Q48, Q49, Q50, Q51, Q52, Q53, Q54, Q55, Q56, Q57, Q58, Q59, Q60, Q61, Q62, Q63, Q64, Q65, Q66, Q67, Q68, Q69]), "depth" : 6.5 * mm, "offsetDistance" : 25 * mm});
        }
        {
            var Q0;
            {var subQ0=sQuery(id+"F0.wireOp",EDGE,"E6");Q0=makeQuery(id+"F1.opExtrude","SWEPT_FACE",FACE,{"disambiguationData":[OSD([subQ0]),TDD([makeQuery(id+"F0.imprint","IMPRINT",EDGE,{"disambiguationData":[TD([[makeQuery(id+"F0.imprint","INTERSECT",VERTEX,{"derivedFrom":[subQ0,sQuery(id+"F0.wireOp",EDGE,"E15")]}),1.0]])],"derivedFrom":subQ0})])]});}
            var Q1;
            {var subQ0=sQuery(id+"F0.wireOp",EDGE,"E40");var subQ1=sQuery(id+"F0.wireOp",EDGE,"E6");Q1=makeQuery(id+"F1.opExtrude","SWEPT_FACE",FACE,{"disambiguationData":[OSD([subQ0]),TDD([makeQuery(id+"F0.imprint","IMPRINT",EDGE,{"disambiguationData":[TD([[makeQuery(id+"F0.imprint","INTERSECT",VERTEX,{"disambiguationData":[OD(0.0)],"derivedFrom":[subQ1,subQ0]}),1.0]])],"derivedFrom":subQ0})])]});}
            var Q2;
            Q2=makeQuery(id+"F1.opExtrude","SWEPT_FACE",FACE,{"disambiguationData":[OSD([sQuery(id+"F0.wireOp",EDGE,"E38")])]});
            var Q3;
            {var subQ0=sQuery(id+"F0.wireOp",EDGE,"E35.1.0");Q3=makeQuery(id+"F1.opExtrude","SWEPT_FACE",FACE,{"disambiguationData":[OSD([subQ0]),TDD([makeQuery(id+"F0.imprint","IMPRINT",EDGE,{"disambiguationData":[TD([[makeQuery(id+"F0.imprint","INTERSECT",VERTEX,{"derivedFrom":[subQ0,sQuery(id+"F0.wireOp",EDGE,"E38")]}),1.0]])],"derivedFrom":subQ0})])]});}
            var Q4;
            {var subQ0=sQuery(id+"F0.wireOp",EDGE,"E6");Q4=makeQuery(id+"F1.opExtrude","SWEPT_FACE",FACE,{"disambiguationData":[OSD([subQ0]),TDD([makeQuery(id+"F0.imprint","IMPRINT",EDGE,{"disambiguationData":[TD([[makeQuery(id+"F0.imprint","INTERSECT",VERTEX,{"derivedFrom":[subQ0,sQuery(id+"F0.wireOp",EDGE,"E38")]}),-1.0]])],"derivedFrom":subQ0})])]});}
            var Q5;
            {var subQ0=sQuery(id+"F0.wireOp",EDGE,"E42.1.1");var subQ1=sQuery(id+"F0.wireOp",EDGE,"E35.1.0");Q5=makeQuery(id+"F1.opExtrude","SWEPT_FACE",FACE,{"disambiguationData":[OSD([subQ0]),TDD([makeQuery(id+"F0.imprint","IMPRINT",EDGE,{"disambiguationData":[TD([[makeQuery(id+"F0.imprint","INTERSECT",VERTEX,{"disambiguationData":[OD(0.0)],"derivedFrom":[subQ1,subQ0]}),-1.0]])],"derivedFrom":subQ0})])]});}
            var Q6;
            {var subQ0=sQuery(id+"F0.wireOp",EDGE,"E35.1.0");Q6=makeQuery(id+"F1.opExtrude","SWEPT_FACE",FACE,{"disambiguationData":[OSD([subQ0]),TDD([makeQuery(id+"F0.imprint","IMPRINT",EDGE,{"disambiguationData":[TD([[makeQuery(id+"F0.imprint","INTERSECT",VERTEX,{"derivedFrom":[sQuery(id+"F0.wireOp",EDGE,"E33.1.0"),subQ0]}),-1.0]])],"derivedFrom":subQ0})])]});}
            var Q7;
            Q7=makeQuery(id+"F1.opExtrude","SWEPT_FACE",FACE,{"disambiguationData":[OSD([sQuery(id+"F0.wireOp",EDGE,"E33.1.0")])]});
            var Q8;
            Q8=makeQuery(id+"F1.opExtrude","SWEPT_FACE",FACE,{"disambiguationData":[OSD([sQuery(id+"F0.wireOp",EDGE,"E32.1.0")])]});
            var Q9;
            Q9=makeQuery(id+"F1.opExtrude","CAP_EDGE",EDGE,{"disambiguationData":[OSD([sQuery(id+"F0.wireOp",EDGE,"E15")])],"isStart":true});
            var Q10;
            Q10=makeQuery(id+"F1.opExtrude","SWEPT_EDGE",EDGE,{"disambiguationData":[OSD([sQuery(id+"F0.wireOp",EDGE,"E6"),sQuery(id+"F0.wireOp",EDGE,"E15")])]});
            var Q11;
            Q11=makeQuery(id+"F1.opExtrude","CAP_EDGE",EDGE,{"disambiguationData":[OSD([sQuery(id+"F0.wireOp",EDGE,"E15")])],"isStart":false});
            var Q12;
            Q12=makeQuery(id+"F1.opExtrude","SWEPT_FACE",FACE,{"disambiguationData":[OSD([sQuery(id+"F0.wireOp",EDGE,"E15")])]});
            var Q13;
            {var subQ0=sQuery(id+"F0.wireOp",EDGE,"E30");Q13=makeQuery(id+"F1.opExtrude","SWEPT_FACE",FACE,{"disambiguationData":[OSD([subQ0]),TDD([makeQuery(id+"F0.imprint","IMPRINT",EDGE,{"disambiguationData":[TD([[makeQuery(id+"F0.imprint","INTERSECT",VERTEX,{"disambiguationData":[OD(0.0)],"derivedFrom":[sQuery(id+"F0.wireOp",EDGE,"E17"),subQ0]}),1.0]])],"derivedFrom":subQ0})])]});}
            var Q14;
            Q14=makeQuery(id+"F1.opExtrude","SWEPT_FACE",FACE,{"disambiguationData":[OSD([sQuery(id+"F0.wireOp",EDGE,"E16.MirrorC")])]});
            var Q15;
            {var subQ0=sQuery(id+"F0.wireOp",EDGE,"E7");Q15=makeQuery(id+"F1.opExtrude","CAP_EDGE",EDGE,{"disambiguationData":[OSD([subQ0]),TDD([makeQuery(id+"F0.imprint","IMPRINT",EDGE,{"disambiguationData":[TD([[makeQuery(id+"F0.imprint","INTERSECT",VERTEX,{"derivedFrom":[subQ0,sQuery(id+"F0.wireOp",EDGE,"E16.MirrorC")]}),-1.0]])],"derivedFrom":subQ0})])],"isStart":true});}
            var Q16;
            {var subQ0=sQuery(id+"F0.wireOp",EDGE,"E30");var subQ1=sQuery(id+"F0.wireOp",EDGE,"E17");Q16=makeQuery(id+"F1.opExtrude","SWEPT_EDGE",EDGE,{"disambiguationData":[OSD([subQ1,subQ0]),TDD([makeQuery(id+"F0.imprint","INTERSECT",VERTEX,{"disambiguationData":[OD(0.0)],"derivedFrom":[subQ1,subQ0]})])]});}
            var Q17;
            Q17=makeQuery(id+"F1.opExtrude","SWEPT_EDGE",EDGE,{"disambiguationData":[OSD([sQuery(id+"F0.wireOp",EDGE,"E15"),sQuery(id+"F0.wireOp",EDGE,"E17")])]});
            var Q18;
            {var subQ0=sQuery(id+"F0.wireOp",EDGE,"E17");Q18=makeQuery(id+"F1.opExtrude","SWEPT_FACE",FACE,{"disambiguationData":[OSD([subQ0]),TDD([makeQuery(id+"F0.imprint","IMPRINT",EDGE,{"disambiguationData":[TD([[makeQuery(id+"F0.imprint","INTERSECT",VERTEX,{"disambiguationData":[OD(1.0)],"derivedFrom":[sQuery(id+"F0.wireOp",EDGE,"E15"),subQ0]}),-1.0]])],"derivedFrom":subQ0})])]});}
            var Q19;
            {var subQ0=sQuery(id+"F0.wireOp",EDGE,"E41.MirrorC");var subQ1=sQuery(id+"F0.wireOp",EDGE,"E7");Q19=makeQuery(id+"F1.opExtrude","SWEPT_FACE",FACE,{"disambiguationData":[OSD([subQ0]),TDD([makeQuery(id+"F0.imprint","IMPRINT",EDGE,{"disambiguationData":[TD([[makeQuery(id+"F0.imprint","INTERSECT",VERTEX,{"disambiguationData":[OD(0.0)],"derivedFrom":[subQ1,subQ0]}),-1.0]])],"derivedFrom":subQ0})])]});}
            var Q20;
            Q20=makeQuery(id+"F1.opExtrude","SWEPT_FACE",FACE,{"disambiguationData":[OSD([sQuery(id+"F0.wireOp",EDGE,"E39.2.0")])]});
            var Q21;
            {var subQ0=sQuery(id+"F0.wireOp",EDGE,"E7");Q21=makeQuery(id+"F1.opExtrude","SWEPT_FACE",FACE,{"disambiguationData":[OSD([subQ0]),TDD([makeQuery(id+"F0.imprint","IMPRINT",EDGE,{"disambiguationData":[TD([[makeQuery(id+"F0.imprint","INTERSECT",VERTEX,{"derivedFrom":[subQ0,sQuery(id+"F0.wireOp",EDGE,"E39.2.0")]}),1.0]])],"derivedFrom":subQ0})])]});}
            var Q22;
            {var subQ0=sQuery(id+"F0.wireOp",EDGE,"E34.2.0");Q22=makeQuery(id+"F1.opExtrude","SWEPT_FACE",FACE,{"disambiguationData":[OSD([subQ0]),TDD([makeQuery(id+"F0.imprint","IMPRINT",EDGE,{"disambiguationData":[TD([[makeQuery(id+"F0.imprint","INTERSECT",VERTEX,{"derivedFrom":[subQ0,sQuery(id+"F0.wireOp",EDGE,"E39.2.0")]}),-1.0]])],"derivedFrom":subQ0})])]});}
            var Q23;
            {var subQ0=sQuery(id+"F0.wireOp",EDGE,"E42.2.0");var subQ1=sQuery(id+"F0.wireOp",EDGE,"E34.2.0");Q23=makeQuery(id+"F1.opExtrude","SWEPT_FACE",FACE,{"disambiguationData":[OSD([subQ0]),TDD([makeQuery(id+"F0.imprint","IMPRINT",EDGE,{"disambiguationData":[TD([[makeQuery(id+"F0.imprint","INTERSECT",VERTEX,{"disambiguationData":[OD(0.0)],"derivedFrom":[subQ1,subQ0]}),1.0]])],"derivedFrom":subQ0})])]});}
            var Q24;
            {var subQ0=sQuery(id+"F0.wireOp",EDGE,"E34.2.0");Q24=makeQuery(id+"F1.opExtrude","SWEPT_FACE",FACE,{"disambiguationData":[OSD([subQ0]),TDD([makeQuery(id+"F0.imprint","IMPRINT",EDGE,{"disambiguationData":[TD([[makeQuery(id+"F0.imprint","INTERSECT",VERTEX,{"derivedFrom":[sQuery(id+"F0.wireOp",EDGE,"E32.2.0"),subQ0]}),1.0]])],"derivedFrom":subQ0})])]});}
            var Q25;
            {var subQ0=sQuery(id+"F0.wireOp",EDGE,"E37.2.8");Q25=makeQuery(id+"F1.opExtrude","SWEPT_FACE",FACE,{"disambiguationData":[OSD([subQ0]),TDD([makeQuery(id+"F0.imprint","IMPRINT",EDGE,{"disambiguationData":[TD([[makeQuery(id+"F0.imprint","INTERSECT",VERTEX,{"disambiguationData":[OD(0.0)],"derivedFrom":[sQuery(id+"F0.wireOp",EDGE,"E37.2.7"),subQ0]}),1.0]])],"derivedFrom":subQ0})])]});}
            var Q26;
            Q26=makeQuery(id+"F1.opExtrude","SWEPT_FACE",FACE,{"disambiguationData":[OSD([sQuery(id+"F0.wireOp",EDGE,"E32.2.0")])]});
            var Q27;
            {var subQ0=sQuery(id+"F0.wireOp",EDGE,"E37.2.7");Q27=makeQuery(id+"F1.opExtrude","SWEPT_FACE",FACE,{"disambiguationData":[OSD([subQ0]),TDD([makeQuery(id+"F0.imprint","IMPRINT",EDGE,{"disambiguationData":[TD([[makeQuery(id+"F0.imprint","INTERSECT",VERTEX,{"disambiguationData":[OD(1.0)],"derivedFrom":[sQuery(id+"F0.wireOp",EDGE,"E32.2.0"),subQ0]}),-1.0]])],"derivedFrom":subQ0})])]});}
            var Q28;
            {var subQ0=sQuery(id+"F0.wireOp",EDGE,"E37.2.10");Q28=makeQuery(id+"F1.opExtrude","SWEPT_FACE",FACE,{"disambiguationData":[OSD([subQ0]),TDD([makeQuery(id+"F0.imprint","IMPRINT",EDGE,{"disambiguationData":[TD([[makeQuery(id+"F0.imprint","INTERSECT",VERTEX,{"disambiguationData":[OD(1.0)],"derivedFrom":[sQuery(id+"F0.wireOp",EDGE,"E33.2.0"),subQ0]}),1.0]])],"derivedFrom":subQ0})])]});}
            var Q29;
            Q29=makeQuery(id+"F1.opExtrude","SWEPT_FACE",FACE,{"disambiguationData":[OSD([sQuery(id+"F0.wireOp",EDGE,"E33.2.0")])]});
            var Q30;
            {var subQ0=sQuery(id+"F0.wireOp",EDGE,"E35.2.0");Q30=makeQuery(id+"F1.opExtrude","SWEPT_FACE",FACE,{"disambiguationData":[OSD([subQ0]),TDD([makeQuery(id+"F0.imprint","IMPRINT",EDGE,{"disambiguationData":[TD([[makeQuery(id+"F0.imprint","INTERSECT",VERTEX,{"derivedFrom":[sQuery(id+"F0.wireOp",EDGE,"E33.2.0"),subQ0]}),-1.0]])],"derivedFrom":subQ0})])]});}
            var Q31;
            {var subQ0=sQuery(id+"F0.wireOp",EDGE,"E42.2.1");var subQ1=sQuery(id+"F0.wireOp",EDGE,"E35.2.0");Q31=makeQuery(id+"F1.opExtrude","SWEPT_EDGE",EDGE,{"disambiguationData":[OSD([subQ1,subQ0]),TDD([makeQuery(id+"F0.imprint","INTERSECT",VERTEX,{"disambiguationData":[OD(1.0)],"derivedFrom":[subQ1,subQ0]})])]});}
            var Q32;
            {var subQ0=sQuery(id+"F0.wireOp",EDGE,"E35.2.0");Q32=makeQuery(id+"F1.opExtrude","SWEPT_FACE",FACE,{"disambiguationData":[OSD([subQ0]),TDD([makeQuery(id+"F0.imprint","IMPRINT",EDGE,{"disambiguationData":[TD([[makeQuery(id+"F0.imprint","INTERSECT",VERTEX,{"derivedFrom":[subQ0,sQuery(id+"F0.wireOp",EDGE,"E39.1.0")]}),1.0]])],"derivedFrom":subQ0})])]});}
            var Q33;
            Q33=makeQuery(id+"F1.opExtrude","SWEPT_FACE",FACE,{"disambiguationData":[OSD([sQuery(id+"F0.wireOp",EDGE,"E39.1.0")])]});
            var Q34;
            {var subQ0=sQuery(id+"F0.wireOp",EDGE,"E34.1.0");Q34=makeQuery(id+"F1.opExtrude","SWEPT_FACE",FACE,{"disambiguationData":[OSD([subQ0]),TDD([makeQuery(id+"F0.imprint","IMPRINT",EDGE,{"disambiguationData":[TD([[makeQuery(id+"F0.imprint","INTERSECT",VERTEX,{"derivedFrom":[sQuery(id+"F0.wireOp",EDGE,"E32.1.0"),subQ0]}),1.0]])],"derivedFrom":subQ0})])]});}
            var Q35;
            {var subQ0=sQuery(id+"F0.wireOp",EDGE,"E37.1.8");Q35=makeQuery(id+"F1.opExtrude","SWEPT_FACE",FACE,{"disambiguationData":[OSD([subQ0]),TDD([makeQuery(id+"F0.imprint","IMPRINT",EDGE,{"disambiguationData":[TD([[makeQuery(id+"F0.imprint","INTERSECT",VERTEX,{"disambiguationData":[OD(0.0)],"derivedFrom":[sQuery(id+"F0.wireOp",EDGE,"E37.1.7"),subQ0]}),1.0]])],"derivedFrom":subQ0})])]});}
            var Q36;
            {var subQ0=sQuery(id+"F0.wireOp",EDGE,"E42.1.0");var subQ1=sQuery(id+"F0.wireOp",EDGE,"E34.1.0");Q36=makeQuery(id+"F1.opExtrude","SWEPT_FACE",FACE,{"disambiguationData":[OSD([subQ0]),TDD([makeQuery(id+"F0.imprint","IMPRINT",EDGE,{"disambiguationData":[TD([[makeQuery(id+"F0.imprint","INTERSECT",VERTEX,{"disambiguationData":[OD(0.0)],"derivedFrom":[subQ1,subQ0]}),1.0]])],"derivedFrom":subQ0})])]});}
            var Q37;
            {var subQ0=sQuery(id+"F0.wireOp",EDGE,"E34.1.0");Q37=makeQuery(id+"F1.opExtrude","SWEPT_FACE",FACE,{"disambiguationData":[OSD([subQ0]),TDD([makeQuery(id+"F0.imprint","IMPRINT",EDGE,{"disambiguationData":[TD([[makeQuery(id+"F0.imprint","INTERSECT",VERTEX,{"derivedFrom":[subQ0,sQuery(id+"F0.wireOp",EDGE,"E39.1.0")]}),-1.0]])],"derivedFrom":subQ0})])]});}
            fillet(context, id + "F2", {"entities" : qUnion([Q0, Q1, Q2, Q3, Q4, Q5, Q6, Q7, Q8, Q9, Q10, Q11, Q12, Q13, Q14, Q15, Q16, Q17, Q18, Q19, Q20, Q21, Q22, Q23, Q24, Q25, Q26, Q27, Q28, Q29, Q30, Q31, Q32, Q33, Q34, Q35, Q36, Q37]), "radius" : 0.5 * mm, "tangentPropagation" : true, "allowEdgeOverflow" : false});
        }
    });
